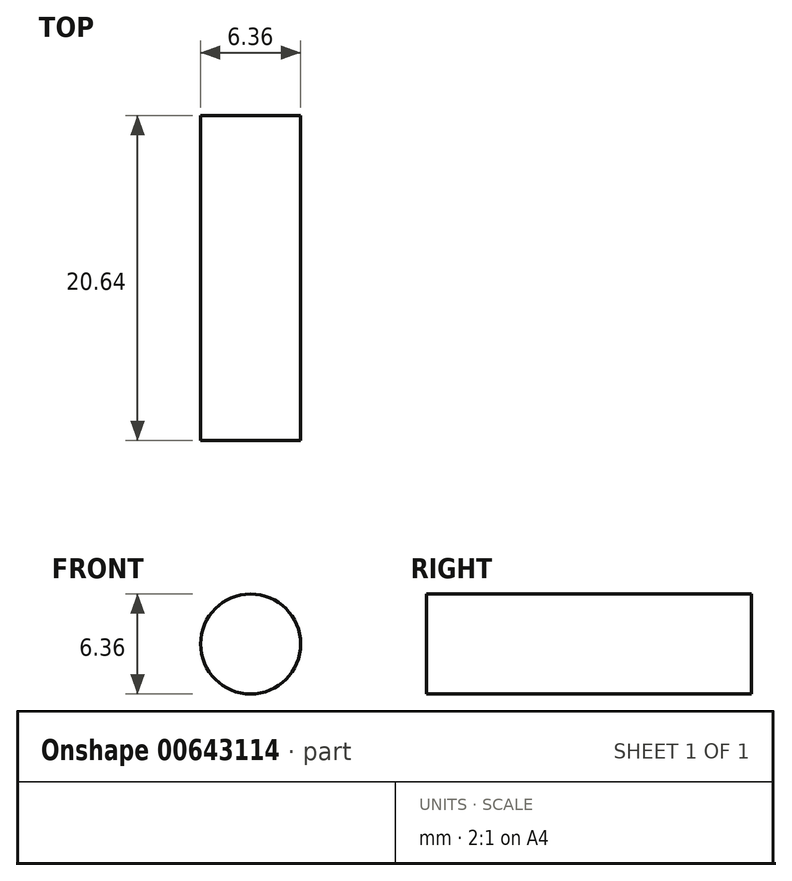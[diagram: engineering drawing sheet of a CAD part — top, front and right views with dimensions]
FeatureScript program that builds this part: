
annotation { "Feature Type Name" : "Feature", "Feature Type Description" : "" }
export const myFeature = defineFeature(function(context is Context, id is Id, definition is map)
    precondition{}
    {
        {
            var Q0;
            Q0=qCreatedBy(makeId("Front.planeOp"),FACE);
            var sketch = newSketch(context, id + "F0", { "sketchPlane" : qUnion([Q0])});
            skCircle(sketch, "E0", {"center": v(0, 0) * mm, "radius": 3.17 * mm});
            skSolve(sketch);
        }
        {
            var Q0;
            Q0 = qSketchRegion(id + "F0", true);
            extrude(context, id + "F1", {"entities" : qUnion([Q0]), "depth" : 20.64 * mm, "offsetDistance" : 25.4 * mm});
        }
    });
